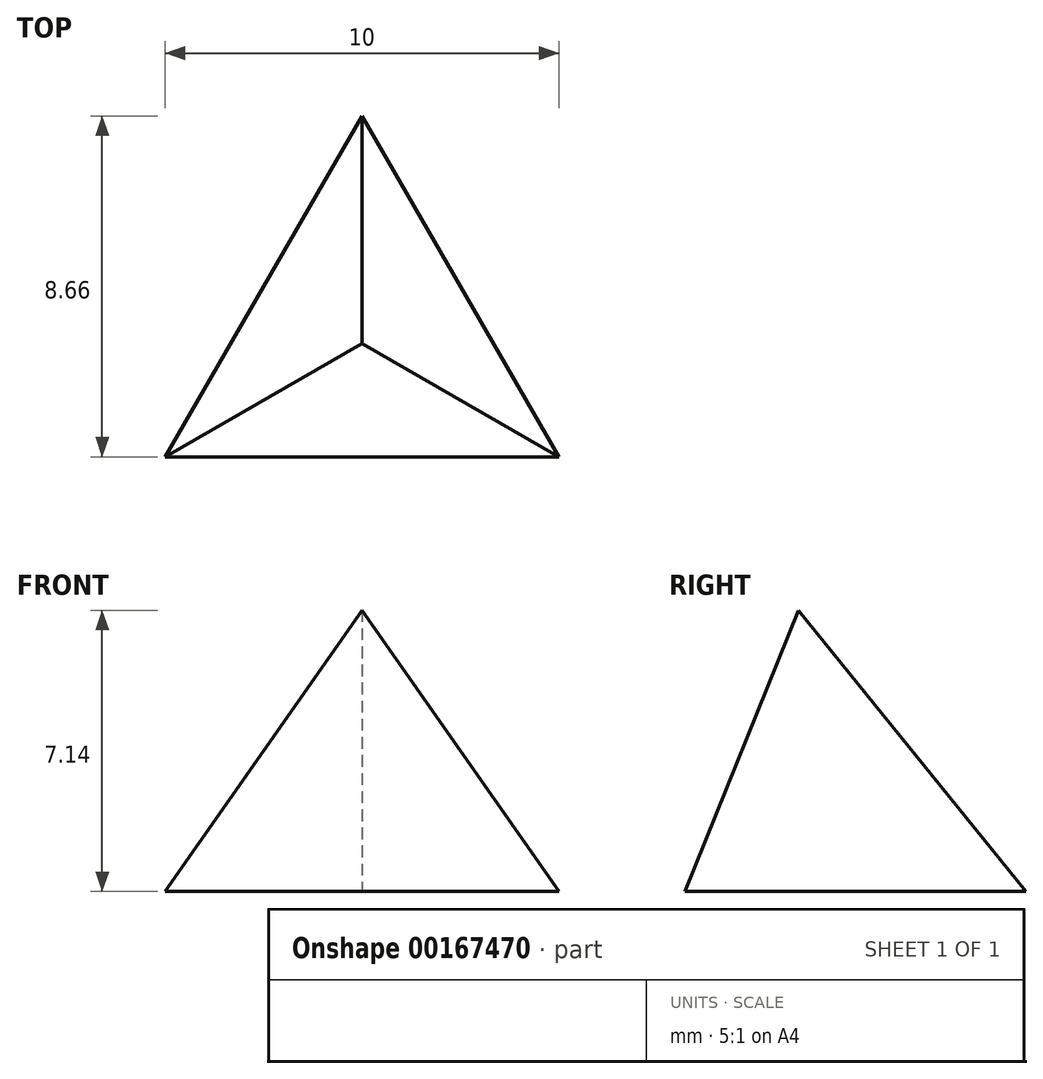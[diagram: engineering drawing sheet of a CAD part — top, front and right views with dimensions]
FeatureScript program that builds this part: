
annotation { "Feature Type Name" : "Feature", "Feature Type Description" : "" }
export const myFeature = defineFeature(function(context is Context, id is Id, definition is map)
    precondition{}
    {
        {
            var Q0;
            Q0=qCreatedBy(makeId("Top.planeOp"),FACE);
            var sketch = newSketch(context, id + "F0", { "sketchPlane" : qUnion([Q0])});
            skLineSegment(sketch, "E0", {"start": v(-5, 0) * mm, "end": v(0, 8.66) * mm});
            skLineSegment(sketch, "E1", {"start": v(0, 8.66) * mm, "end": v(5, 0) * mm});
            skLineSegment(sketch, "E2", {"start": v(5, 0) * mm, "end": v(-5, 0) * mm});
            skSolve(sketch);
        }
        {
            var Q0;
            Q0=makeQuery(id+"F0.imprint","IMPRINT",FACE,{"disambiguationData":[TD([[makeQuery(id+"F0.imprint","IMPRINT",EDGE,{"derivedFrom":sQuery(id+"F0.wireOp",EDGE,"E0")}),-1.0]])]});
            extrude(context, id + "F1", {"entities" : qUnion([Q0]), "depth" : 25 * mm, "hasDraft" : true, "draftAngle" : 22 * degree, "draftPullDirection" : true});
        }
    });
